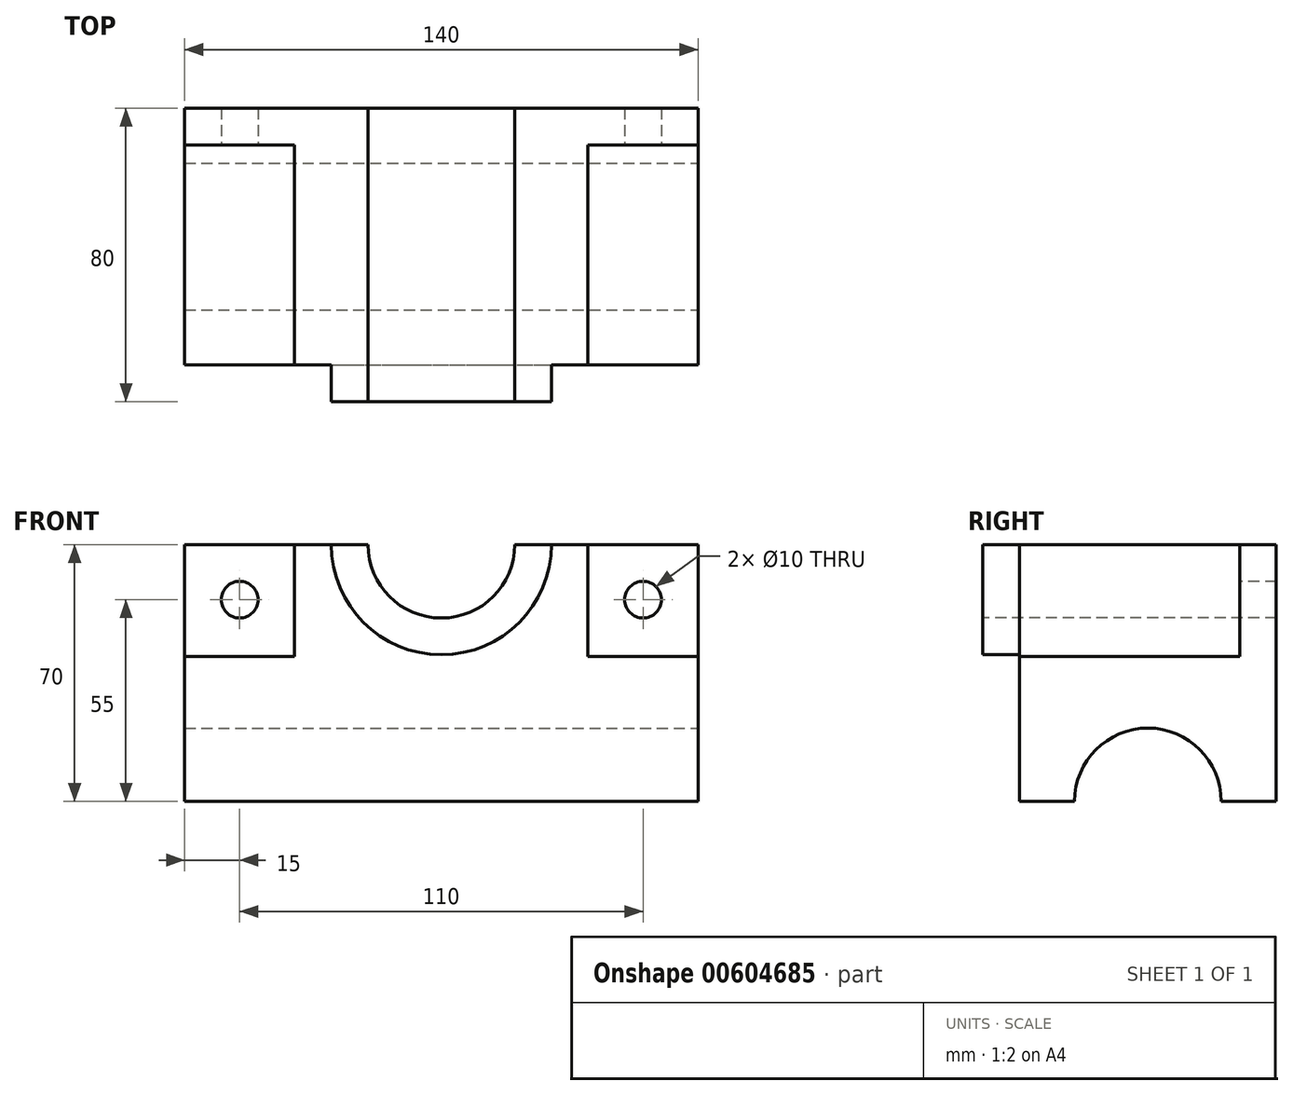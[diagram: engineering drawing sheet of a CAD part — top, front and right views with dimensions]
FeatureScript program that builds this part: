
annotation { "Feature Type Name" : "Feature", "Feature Type Description" : "" }
export const myFeature = defineFeature(function(context is Context, id is Id, definition is map)
    precondition{}
    {
        {
            var Q0;
            Q0=qCreatedBy(makeId("Front.planeOp"),FACE);
            var sketch = newSketch(context, id + "F0", { "sketchPlane" : qUnion([Q0])});
            skLineSegment(sketch, "E0", {"start": v(0, -70) * mm, "end": v(70, -70) * mm});
            skLineSegment(sketch, "E1", {"start": v(70, -70) * mm, "end": v(70, 0) * mm});
            skLineSegment(sketch, "E2", {"start": v(70, 0) * mm, "end": v(20, 0) * mm});
            skLineSegment(sketch, "E3", {"start": v(0, -20) * mm, "end": v(0, -70) * mm});
            skArc(sketch, "E4", {"start": v(0, -20) * mm, "mid": v(14.14, -14.14) * mm, "end": v(20, 0) * mm});
            skLineSegment(sketch, "E5", {"start": v(0, 18.1) * mm, "end": v(0, -79.28) * mm, "construction": true});
            skSolve(sketch);
        }
        {
            var Q0;
            Q0=makeQuery(id+"F0.imprint","IMPRINT",FACE,{"disambiguationData":[TD([[makeQuery(id+"F0.imprint","IMPRINT",EDGE,{"derivedFrom":sQuery(id+"F0.wireOp",EDGE,"E0")}),1.0]])]});
            extrude(context, id + "F1", {"entities" : qUnion([Q0]), "oppositeDirection" : true, "depth" : 70 * mm, "offsetDistance" : 25 * mm});
        }
        {
            var Q0;
            Q0=makeQuery(id+"F1.opExtrude","CAP_FACE",FACE,{"disambiguationData":[OSD([sQuery(id+"F0.wireOp",EDGE,"Yuq5ac2I-y3WY-IghG-N2Y8-SBjBaCPQ4lPd"),sQuery(id+"F0.wireOp",EDGE,"E0"),sQuery(id+"F0.wireOp",EDGE,"E1"),sQuery(id+"F0.wireOp",EDGE,"E2"),sQuery(id+"F0.wireOp",EDGE,"E3")])],"isStart":true});
            var sketch = newSketch(context, id + "F2", { "sketchPlane" : qUnion([Q0])});
            skLineSegment(sketch, "E6.bottom", {"start": v(70, 0) * mm, "end": v(40, 0) * mm});
            skLineSegment(sketch, "E6.top", {"start": v(70, -30.53) * mm, "end": v(40, -30.53) * mm});
            skLineSegment(sketch, "E6.left", {"start": v(70, 0) * mm, "end": v(70, -30.53) * mm});
            skLineSegment(sketch, "E6.right", {"start": v(40, 0) * mm, "end": v(40, -30.53) * mm});
            skSolve(sketch);
        }
        {
            var Q0;
            Q0 = qSketchRegion(id + "F2", true);
            extrude(context, id + "F3", {"entities" : qUnion([Q0]), "operationType" : NewBodyOperationType.REMOVE, "oppositeDirection" : true, "depth" : 60 * mm, "offsetDistance" : 25 * mm});
        }
        {
            var Q0;
            Q0=makeQuery(id+"F3.boolean.opBoolean","COPY",FACE,{"derivedFrom":makeQuery(id+"F3.opExtrude","CAP_FACE",FACE,{"disambiguationData":[OSD([sQuery(id+"F2.wireOp",EDGE,"E6.bottom"),sQuery(id+"F2.wireOp",EDGE,"E6.top"),sQuery(id+"F2.wireOp",EDGE,"E6.left"),sQuery(id+"F2.wireOp",EDGE,"E6.right")])],"isStart":false})});
            var sketch = newSketch(context, id + "F4", { "sketchPlane" : qUnion([Q0])});
            skCircle(sketch, "E7", {"center": v(55, -15) * mm, "radius": 5 * mm});
            skSolve(sketch);
        }
        {
            var Q0;
            Q0 = qSketchRegion(id + "F4", true);
            extrude(context, id + "F5", {"entities" : qUnion([Q0]), "operationType" : NewBodyOperationType.REMOVE, "endBound" : BoundingType.THROUGH_ALL, "oppositeDirection" : true, "depth" : 25 * mm, "offsetDistance" : 25 * mm});
        }
        {
            var Q0;
            Q0=makeQuery(id+"F1.opExtrude","SWEPT_FACE",FACE,{"disambiguationData":[OSD([sQuery(id+"F0.wireOp",EDGE,"E1")])]});
            var sketch = newSketch(context, id + "F6", { "sketchPlane" : qUnion([Q0])});
            skCircle(sketch, "E8", {"center": v(35, -70) * mm, "radius": 20 * mm});
            skSolve(sketch);
        }
        {
            var Q0;
            Q0 = qSketchRegion(id + "F6", true);
            extrude(context, id + "F7", {"entities" : qUnion([Q0]), "operationType" : NewBodyOperationType.REMOVE, "endBound" : BoundingType.THROUGH_ALL, "oppositeDirection" : true, "depth" : 25 * mm, "offsetDistance" : 25 * mm});
        }
        {
            var Q0;
            Q0=makeQuery(id+"F1.opExtrude","CAP_FACE",FACE,{"disambiguationData":[OSD([sQuery(id+"F0.wireOp",EDGE,"E0"),sQuery(id+"F0.wireOp",EDGE,"E1"),sQuery(id+"F0.wireOp",EDGE,"E2"),sQuery(id+"F0.wireOp",EDGE,"E3"),sQuery(id+"F0.wireOp",EDGE,"E4")])],"isStart":true});
            var sketch = newSketch(context, id + "F8", { "sketchPlane" : qUnion([Q0])});
            skArc(sketch, "E9.0", {"start": v(0, -20) * mm, "mid": v(14.14, -14.14) * mm, "end": v(20, 0) * mm});
            skLineSegment(sketch, "E10.0", {"start": v(40, 0) * mm, "end": v(20, 0) * mm});
            skLineSegment(sketch, "E11.0", {"start": v(0, -20) * mm, "end": v(0, -70) * mm});
            skArc(sketch, "E12", {"start": v(0, -30) * mm, "mid": v(21.21, -21.21) * mm, "end": v(30, 0) * mm});
            skSolve(sketch);
        }
        {
            var Q0;
            {var subQ0=sQuery(id+"F8.wireOp",EDGE,"E9.0");Q0=makeQuery(id+"F8.imprint","IMPRINT",FACE,{"disambiguationData":[TD([[makeQuery(id+"F8.imprint","IMPRINT",EDGE,{"derivedFrom":subQ0}),-1.0]])]});}
            extrude(context, id + "F9", {"entities" : qUnion([Q0]), "operationType" : NewBodyOperationType.ADD, "depth" : 10 * mm, "offsetDistance" : 25 * mm});
        }
        {
            var Q0;
            Q0=makeQuery(id+"F1.opExtrude","SWEPT_BODY",BODY,{"disambiguationData":[OSD([sQuery(id+"F0.wireOp",EDGE,"E0"),sQuery(id+"F0.wireOp",EDGE,"E1"),sQuery(id+"F0.wireOp",EDGE,"E2"),sQuery(id+"F0.wireOp",EDGE,"E3"),sQuery(id+"F0.wireOp",EDGE,"E4")])]});
            var Q1;
            Q1=qCreatedBy(makeId("Right.planeOp"),FACE);
            mirror(context, id + "F10", {"operationType" : NewBodyOperationType.ADD, "entities" : qUnion([Q0]), "mirrorPlane" : qUnion([Q1])});
        }
    });
